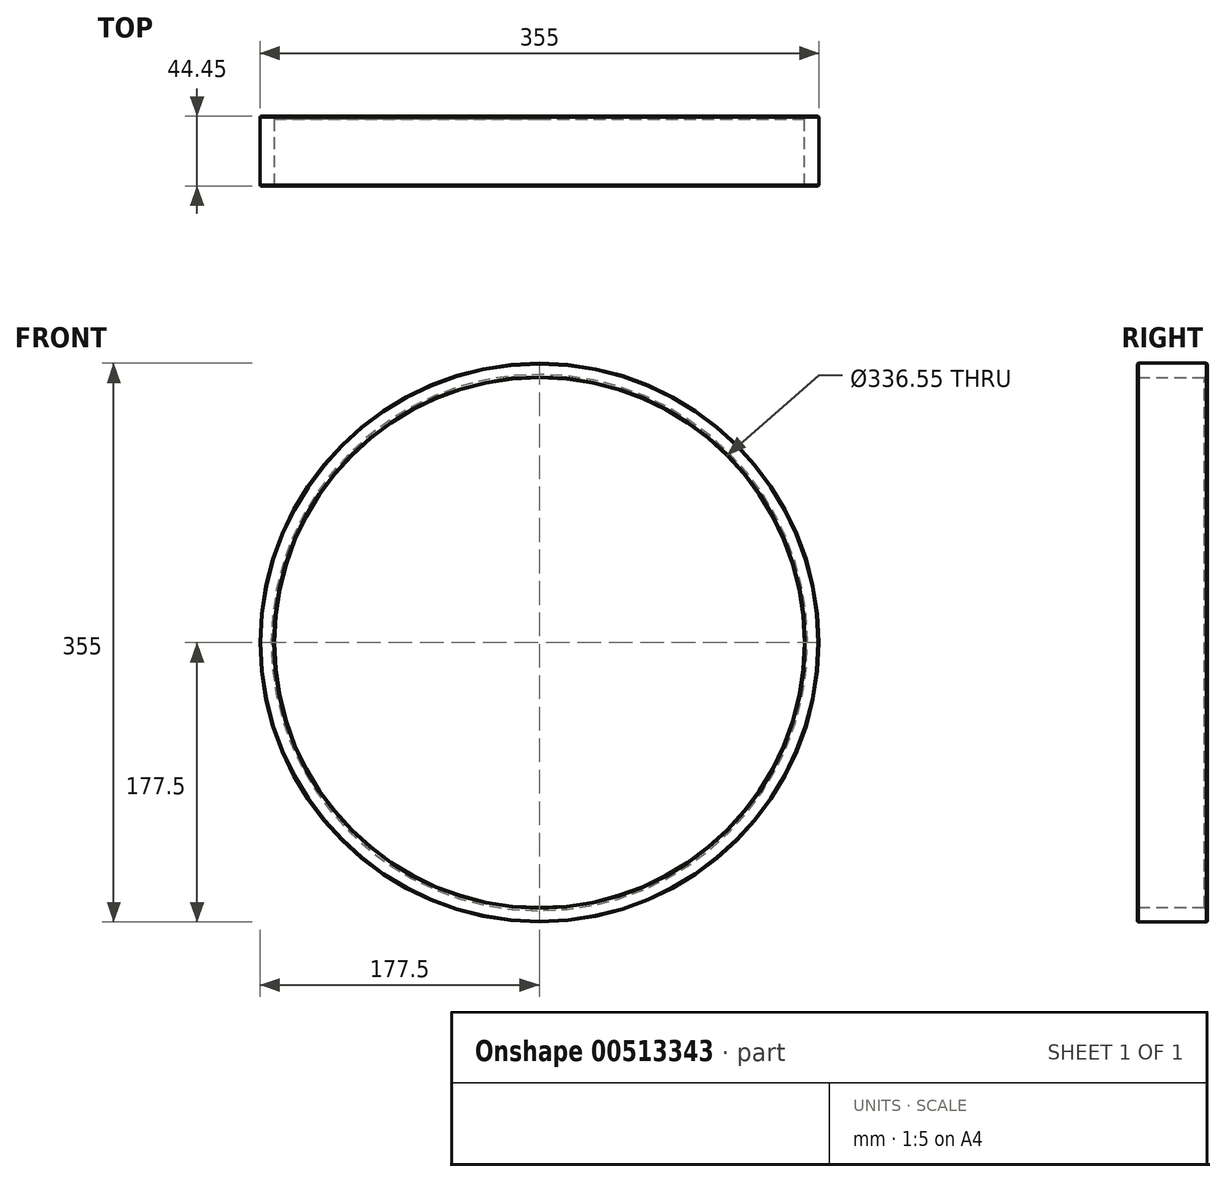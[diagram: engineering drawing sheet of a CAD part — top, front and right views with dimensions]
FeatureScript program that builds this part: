
annotation { "Feature Type Name" : "Feature", "Feature Type Description" : "" }
export const myFeature = defineFeature(function(context is Context, id is Id, definition is map)
    precondition{}
    {
        {
            var Q0;
            Q0=qCreatedBy(makeId("Front.planeOp"),FACE);
            var sketch = newSketch(context, id + "F0", { "sketchPlane" : qUnion([Q0])});
            skCircle(sketch, "E0", {"center": v(0, 0) * mm, "radius": 168.28 * mm});
            skCircle(sketch, "E1", {"center": v(0, 0) * mm, "radius": 177.5 * mm});
            skSolve(sketch);
        }
        {
            var Q0;
            Q0=makeQuery(id+"F0.imprint","IMPRINT",FACE,{"disambiguationData":[TD([[makeQuery(id+"F0.imprint","IMPRINT",EDGE,{"derivedFrom":sQuery(id+"F0.wireOp",EDGE,"E0")}),-1.0]])]});
            extrude(context, id + "F1", {"entities" : qUnion([Q0]), "depth" : 44.45 * mm});
        }
        {
            var Q0;
            Q0=makeQuery(id+"F1.opExtrude","CAP_EDGE",EDGE,{"disambiguationData":[OSD([sQuery(id+"F0.wireOp",EDGE,"E0")])],"isStart":true});
            chamfer(context, id + "F2", {"entities" : qUnion([Q0]), "width" : 2.03 * mm, "tangentPropagation" : true});
        }
        {
            var Q0;
            Q0=makeQuery(id+"F1.opExtrude","CAP_EDGE",EDGE,{"disambiguationData":[OSD([sQuery(id+"F0.wireOp",EDGE,"E0")])],"isStart":false});
            var Q1;
            Q1=makeQuery(id+"F1.opExtrude","CAP_EDGE",EDGE,{"disambiguationData":[OSD([sQuery(id+"F0.wireOp",EDGE,"E1")])],"isStart":false});
            var Q2;
            Q2=makeQuery(id+"F1.opExtrude","CAP_EDGE",EDGE,{"disambiguationData":[OSD([sQuery(id+"F0.wireOp",EDGE,"E1")])],"isStart":true});
            chamfer(context, id + "F3", {"entities" : qUnion([Q0, Q1, Q2]), "width" : 0.5 * mm, "tangentPropagation" : true});
        }
    });
